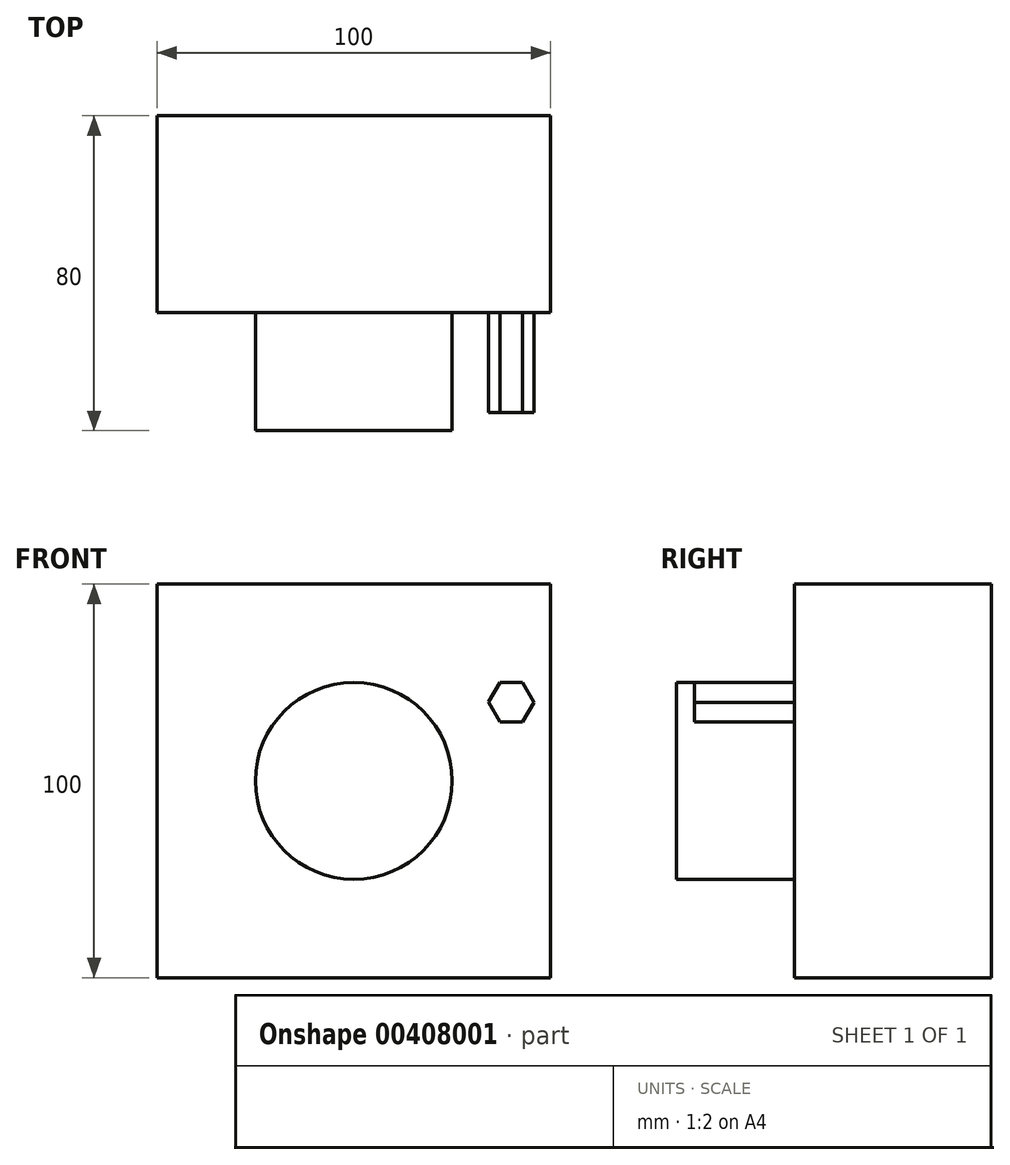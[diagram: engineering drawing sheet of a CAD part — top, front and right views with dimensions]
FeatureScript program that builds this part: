
annotation { "Feature Type Name" : "Feature", "Feature Type Description" : "" }
export const myFeature = defineFeature(function(context is Context, id is Id, definition is map)
    precondition{}
    {
        {
            var Q0;
            Q0=qCreatedBy(makeId("Front.planeOp"),FACE);
            var sketch = newSketch(context, id + "F0", { "sketchPlane" : qUnion([Q0])});
            skLineSegment(sketch, "E0.bottom", {"start": v(50, 50) * mm, "end": v(-50, 50) * mm});
            skLineSegment(sketch, "E0.top", {"start": v(50, -50) * mm, "end": v(-50, -50) * mm});
            skLineSegment(sketch, "E0.left", {"start": v(50, 50) * mm, "end": v(50, -50) * mm});
            skLineSegment(sketch, "E0.right", {"start": v(-50, 50) * mm, "end": v(-50, -50) * mm});
            skPoint(sketch, "E0.middle", {"position": v(0, 0) * mm});
            skSolve(sketch);
        }
        {
            var Q0;
            Q0 = qSketchRegion(id + "F0", true);
            extrude(context, id + "F1", {"entities" : qUnion([Q0]), "depth" : 50 * mm});
        }
        {
            var Q0;
            Q0=makeQuery(id+"F1.opExtrude","CAP_FACE",FACE,{"disambiguationData":[OSD([sQuery(id+"F0.wireOp",EDGE,"E0.bottom"),sQuery(id+"F0.wireOp",EDGE,"E0.top"),sQuery(id+"F0.wireOp",EDGE,"E0.left"),sQuery(id+"F0.wireOp",EDGE,"E0.right")])],"isStart":false});
            var sketch = newSketch(context, id + "F2", { "sketchPlane" : qUnion([Q0])});
            skCircle(sketch, "E1", {"center": v(0, 0) * mm, "radius": 25 * mm});
            skSolve(sketch);
        }
        {
            var Q0;
            Q0 = qSketchRegion(id + "F2", true);
            extrude(context, id + "F3", {"entities" : qUnion([Q0]), "operationType" : NewBodyOperationType.ADD, "depth" : 30 * mm});
        }
        {
            var Q0;
            Q0=makeQuery(id+"F1.opExtrude","CAP_FACE",FACE,{"disambiguationData":[OSD([sQuery(id+"F0.wireOp",EDGE,"E0.bottom"),sQuery(id+"F0.wireOp",EDGE,"E0.top"),sQuery(id+"F0.wireOp",EDGE,"E0.left"),sQuery(id+"F0.wireOp",EDGE,"E0.right")])],"isStart":false});
            var sketch = newSketch(context, id + "F4", { "sketchPlane" : qUnion([Q0])});
            skCircle(sketch, "E2.cCircle", {"center": v(40, 20) * mm, "radius": 5.77 * mm, "construction": true});
            skLineSegment(sketch, "E2.0", {"start": v(42.9, 24.99) * mm, "end": v(45.77, 19.98) * mm});
            skLineSegment(sketch, "E2.1", {"start": v(45.77, 19.98) * mm, "end": v(42.87, 14.99) * mm});
            skLineSegment(sketch, "E2.2", {"start": v(42.87, 14.99) * mm, "end": v(37.1, 15.01) * mm});
            skLineSegment(sketch, "E2.3", {"start": v(37.1, 15.01) * mm, "end": v(34.23, 20.02) * mm});
            skLineSegment(sketch, "E2.4", {"start": v(34.23, 20.02) * mm, "end": v(37.13, 25.01) * mm});
            skLineSegment(sketch, "E2.5", {"start": v(37.13, 25.01) * mm, "end": v(42.9, 24.99) * mm});
            skSolve(sketch);
        }
        {
            var Q0;
            Q0 = qSketchRegion(id + "F4", true);
            extrude(context, id + "F5", {"entities" : qUnion([Q0]), "operationType" : NewBodyOperationType.ADD, "depth" : 25.4 * mm});
        }
    });
